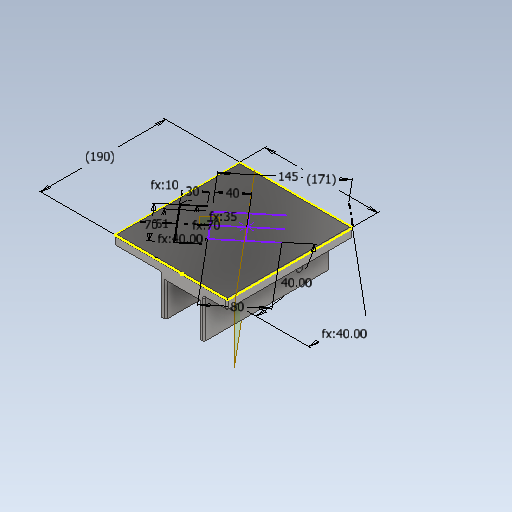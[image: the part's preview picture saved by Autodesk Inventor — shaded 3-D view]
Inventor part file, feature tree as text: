
AUTODESK INVENTOR PART (.ipt)
format: ipt  version: 2021 (Build 250183000, 183)  size: 245,248 bytes
history: native  units: mm
features: sketch x4, extrude x3, other x2, plane x2, hole x1, fillet x1, chamfer x1
ambient origin geometry x8: Origin, YZ Plane, XZ Plane, XY Plane, X Axis, Y Axis, Z Axis, Center Point
bodies: Solid1 (feature_tree)
feature tree (14):
  extrude  "clamp_base"  Depth=66.0mm
  extrude  "clamp_extrusion"  TaperAngle=0.0deg  [1 undecoded]
  extrude  "platform"  Depth=50.0mm
  hole  "clampHole"  [1 undecoded]
  other  "tabWeld"
  plane  "Work Plane4"
  other  "reelWeld"
  fillet  "Fillet1"  [1 undecoded]
  chamfer  "Chamfer1"  Distance=1149.0mm
  plane  "Work Plane5"
  sketch  "Sketch1"  dims[d0=58.0mm d1=66.0mm]
  sketch  "Sketch2"  dims[d2=33.0mm d3=0.0mm]
  sketch  "Sketch4"  dims[d4=190.0mm d5=0.0mm d6=50.0mm]
  sketch  "Sketch8"  dims[d7=50.0mm d8=25.0mm d9=0.0mm d10=0.0mm d12=1149.0mm d13=15.0mm d14=0.0mm d15=51.0mm d35=0.0mm d36=0.0mm d37=70.0mm d38=35.0mm d51=45.0mm d53=10.0mm d54=6.0mm d55=4.0mm d56=2.0mm d57=90.0deg d58=8.0mm d59=20.594885mm d60=100.0mm d61=190.0mm d63=80.0mm d64=51.0mm d67=6.981317mm d68=171.0mm d70=40.0mm d71=190.0mm d73=90.0deg d74=10.0mm d75=6.981317mm d77=30.0mm d78=70.0mm d79=70.0mm d81=2.0mm d82=2.0mm d83=2.0mm d84=45.0deg d86=35.0mm d87=10.0mm d88=6.981317mm d89=145.0mm]
note: 3 required parameter values undecoded (feature->parameter linkage not recoverable at this tier; creation-order binding heuristic only, values carry confidence <= 0.55)
